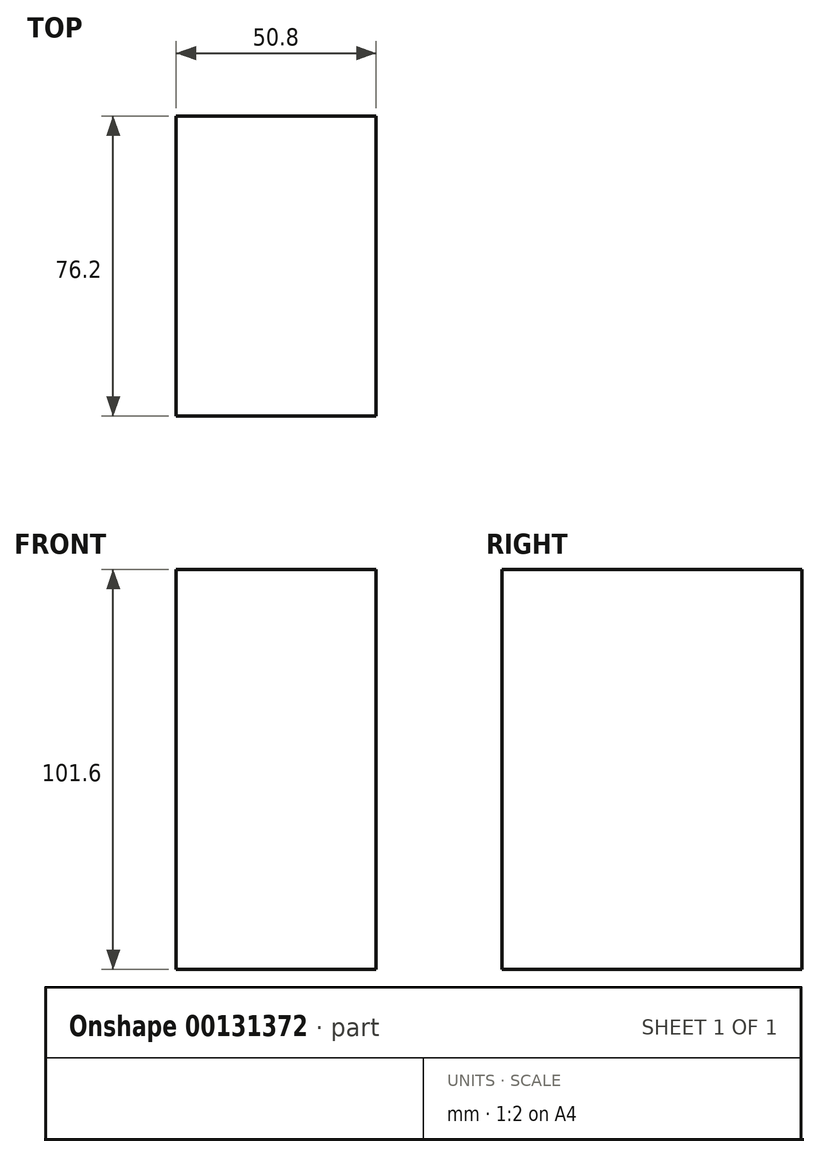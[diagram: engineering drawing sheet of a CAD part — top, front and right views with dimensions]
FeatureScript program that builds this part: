
annotation { "Feature Type Name" : "Feature", "Feature Type Description" : "" }
export const myFeature = defineFeature(function(context is Context, id is Id, definition is map)
    precondition{}
    {
        {
            var Q0;
            Q0=qCreatedBy(makeId("Front.planeOp"),FACE);
            var sketch = newSketch(context, id + "F0", { "sketchPlane" : qUnion([Q0])});
            skLineSegment(sketch, "E0.bottom", {"start": v(-25.4, 50.8) * mm, "end": v(25.4, 50.8) * mm});
            skLineSegment(sketch, "E0.top", {"start": v(-25.4, -50.8) * mm, "end": v(25.4, -50.8) * mm});
            skLineSegment(sketch, "E0.left", {"start": v(-25.4, 50.8) * mm, "end": v(-25.4, -50.8) * mm});
            skLineSegment(sketch, "E0.right", {"start": v(25.4, 50.8) * mm, "end": v(25.4, -50.8) * mm});
            skPoint(sketch, "E0.middle", {"position": v(0, 0) * mm});
            skSolve(sketch);
        }
        {
            var Q0;
            Q0 = qSketchRegion(id + "F0", true);
            extrude(context, id + "F1", {"entities" : qUnion([Q0]), "depth" : 76.2 * mm});
        }
    });
